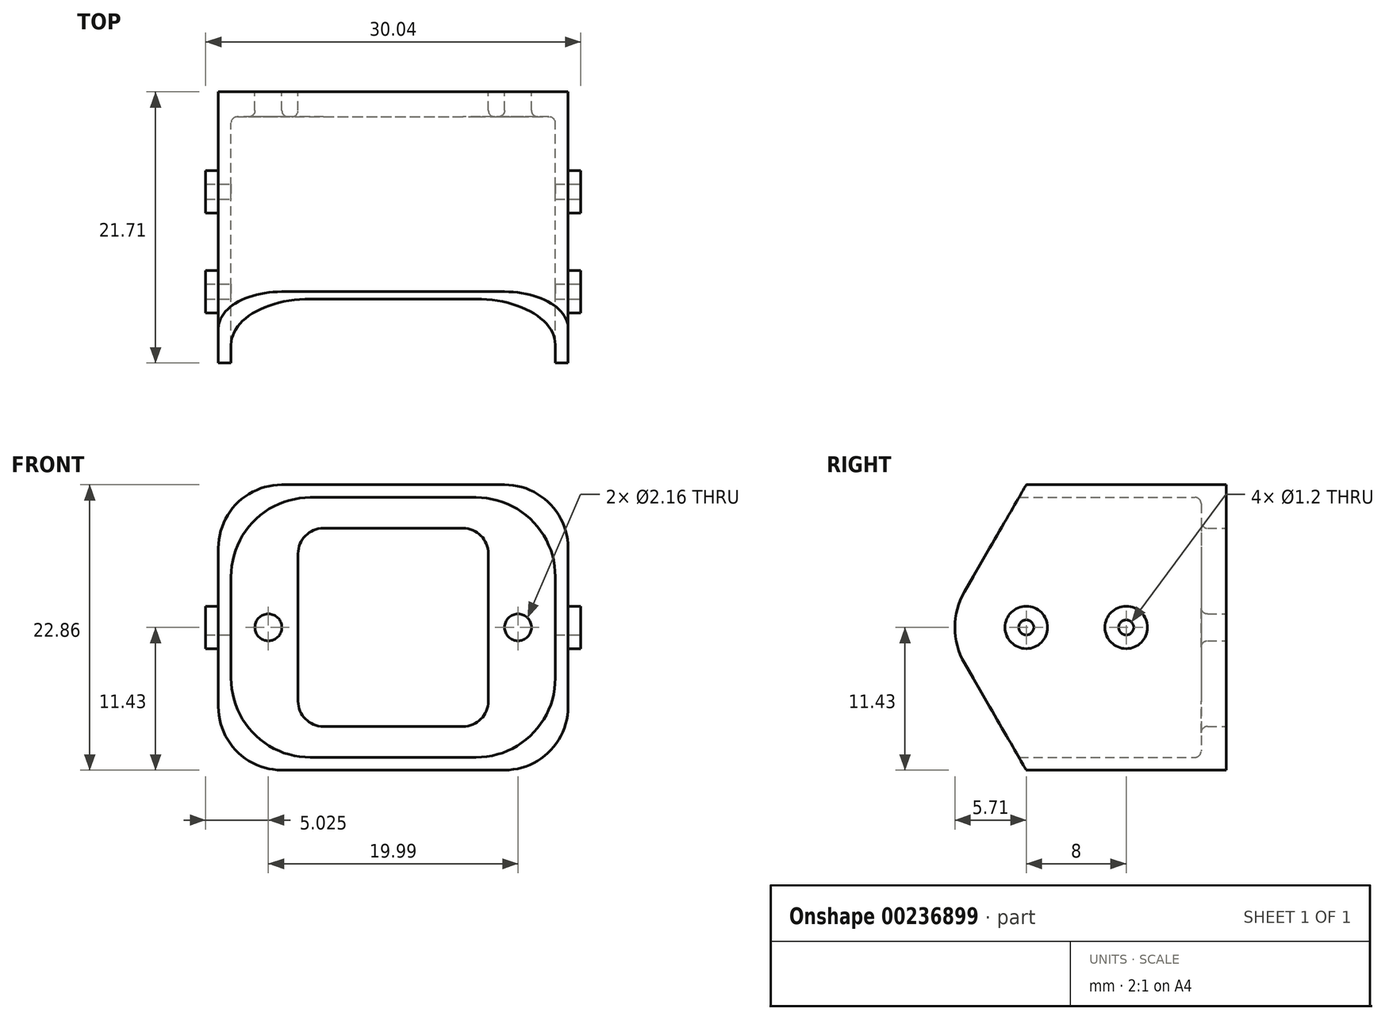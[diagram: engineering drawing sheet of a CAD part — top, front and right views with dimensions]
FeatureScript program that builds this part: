
annotation { "Feature Type Name" : "Feature", "Feature Type Description" : "" }
export const myFeature = defineFeature(function(context is Context, id is Id, definition is map)
    precondition{}
    {
        {
            var Q0;
            Q0=qCreatedBy(makeId("Front.planeOp"),FACE);
            var sketch = newSketch(context, id + "F0", { "sketchPlane" : qUnion([Q0])});
            skLineSegment(sketch, "E0.bottom", {"start": v(-8.92, 11.43) * mm, "end": v(8.92, 11.43) * mm});
            skLineSegment(sketch, "E0.top", {"start": v(-8.92, -11.43) * mm, "end": v(8.92, -11.43) * mm});
            skLineSegment(sketch, "E0.left", {"start": v(-14, 6.35) * mm, "end": v(-14, -6.35) * mm});
            skLineSegment(sketch, "E0.right", {"start": v(14, 6.35) * mm, "end": v(14, -6.35) * mm});
            skPoint(sketch, "E0.middle", {"position": v(0, 0) * mm});
            skLineSegment(sketch, "E1.bottom", {"start": v(-5.59, 7.94) * mm, "end": v(5.59, 7.94) * mm});
            skLineSegment(sketch, "E1.top", {"start": v(-5.59, -7.94) * mm, "end": v(5.59, -7.94) * mm});
            skLineSegment(sketch, "E1.left", {"start": v(-7.62, 5.9) * mm, "end": v(-7.62, -5.9) * mm});
            skLineSegment(sketch, "E1.right", {"start": v(7.62, 5.9) * mm, "end": v(7.62, -5.9) * mm});
            skCircle(sketch, "E2", {"center": v(0, 0) * mm, "radius": 10 * mm, "construction": true});
            skCircle(sketch, "E3", {"center": v(-10, 0) * mm, "radius": 1.08 * mm});
            skCircle(sketch, "E4", {"center": v(10, 0) * mm, "radius": 1.08 * mm});
            skPoint(sketch, "E4.centerSnap0", {"position": v(7.62, 0) * mm});
            skPoint(sketch, "E5.visualSharp", {"position": v(-7.62, 7.94) * mm});
            skArc(sketch, "E5.filletArc", {"start": v(-5.59, 7.94) * mm, "mid": v(-7.02, 7.34) * mm, "end": v(-7.62, 5.9) * mm});
            skPoint(sketch, "E6.visualSharp", {"position": v(7.62, 7.94) * mm});
            skArc(sketch, "E6.filletArc", {"start": v(7.62, 5.9) * mm, "mid": v(7.02, 7.34) * mm, "end": v(5.59, 7.94) * mm});
            skPoint(sketch, "E7.visualSharp", {"position": v(7.62, -7.94) * mm});
            skArc(sketch, "E7.filletArc", {"start": v(5.59, -7.94) * mm, "mid": v(7.02, -7.34) * mm, "end": v(7.62, -5.9) * mm});
            skPoint(sketch, "E8.visualSharp", {"position": v(-7.62, -7.94) * mm});
            skArc(sketch, "E8.filletArc", {"start": v(-7.62, -5.9) * mm, "mid": v(-7.02, -7.34) * mm, "end": v(-5.59, -7.94) * mm});
            skPoint(sketch, "E9.visualSharp", {"position": v(-14, 11.43) * mm});
            skArc(sketch, "E9.filletArc", {"start": v(-8.92, 11.43) * mm, "mid": v(-12.51, 9.94) * mm, "end": v(-14, 6.35) * mm});
            skPoint(sketch, "E10.visualSharp", {"position": v(-14, -11.43) * mm});
            skArc(sketch, "E10.filletArc", {"start": v(-14, -6.35) * mm, "mid": v(-12.51, -9.94) * mm, "end": v(-8.92, -11.43) * mm});
            skPoint(sketch, "E11.visualSharp", {"position": v(14, -11.43) * mm});
            skArc(sketch, "E11.filletArc", {"start": v(8.92, -11.43) * mm, "mid": v(12.51, -9.94) * mm, "end": v(14, -6.35) * mm});
            skPoint(sketch, "E12.visualSharp", {"position": v(14, 11.43) * mm});
            skArc(sketch, "E12.filletArc", {"start": v(14, 6.35) * mm, "mid": v(12.51, 9.94) * mm, "end": v(8.92, 11.43) * mm});
            skSolve(sketch);
        }
        {
            var Q0;
            Q0=qSketchRegion(id+"F0",true);
            extrude(context, id + "F1", {"entities" : qUnion([Q0]), "depth" : 2 * mm});
        }
        {
            var Q0;
            Q0=makeQuery(id+"F1.opExtrude","CAP_FACE",FACE,{"disambiguationData":[OSD([sQuery(id+"F0.wireOp",EDGE,"E0.bottom"),sQuery(id+"F0.wireOp",EDGE,"E0.top"),sQuery(id+"F0.wireOp",EDGE,"E0.left"),sQuery(id+"F0.wireOp",EDGE,"E0.right"),sQuery(id+"F0.wireOp",EDGE,"E1.bottom"),sQuery(id+"F0.wireOp",EDGE,"E1.top"),sQuery(id+"F0.wireOp",EDGE,"E1.left"),sQuery(id+"F0.wireOp",EDGE,"E1.right"),sQuery(id+"F0.wireOp",EDGE,"E3"),sQuery(id+"F0.wireOp",EDGE,"E4"),sQuery(id+"F0.wireOp",EDGE,"E5.filletArc"),sQuery(id+"F0.wireOp",EDGE,"E6.filletArc"),sQuery(id+"F0.wireOp",EDGE,"E7.filletArc"),sQuery(id+"F0.wireOp",EDGE,"E8.filletArc"),sQuery(id+"F0.wireOp",EDGE,"E9.filletArc"),sQuery(id+"F0.wireOp",EDGE,"E10.filletArc"),sQuery(id+"F0.wireOp",EDGE,"E11.filletArc"),sQuery(id+"F0.wireOp",EDGE,"E12.filletArc")])],"isStart":false});
            var sketch = newSketch(context, id + "F2", { "sketchPlane" : qUnion([Q0])});
            skLineSegment(sketch, "E13.0", {"start": v(-8.92, 11.43) * mm, "end": v(8.92, 11.43) * mm});
            skLineSegment(sketch, "E14.0", {"start": v(-14, 6.35) * mm, "end": v(-14, -6.35) * mm});
            skPoint(sketch, "E14.1", {"position": v(-12.51, 9.94) * mm});
            skArc(sketch, "E15.0", {"start": v(-8.92, 11.43) * mm, "mid": v(-12.51, 9.94) * mm, "end": v(-14, 6.35) * mm});
            skArc(sketch, "E16.0", {"start": v(14, 6.35) * mm, "mid": v(12.51, 9.94) * mm, "end": v(8.92, 11.43) * mm});
            skLineSegment(sketch, "E17.0", {"start": v(14, 6.35) * mm, "end": v(14, -6.35) * mm});
            skArc(sketch, "E18.0", {"start": v(8.92, -11.43) * mm, "mid": v(12.51, -9.94) * mm, "end": v(14, -6.35) * mm});
            skLineSegment(sketch, "E19.0", {"start": v(-8.92, -11.43) * mm, "end": v(8.92, -11.43) * mm});
            skArc(sketch, "E20.0", {"start": v(-14, -6.35) * mm, "mid": v(-12.51, -9.94) * mm, "end": v(-8.92, -11.43) * mm});
            skLineSegment(sketch, "E21.0", {"start": v(-6.64, 10.41) * mm, "end": v(6.64, 10.41) * mm});
            skLineSegment(sketch, "E22.0", {"start": v(12.99, 4.06) * mm, "end": v(12.99, -4.06) * mm});
            skLineSegment(sketch, "E23.0", {"start": v(-12.99, 4.06) * mm, "end": v(-12.99, -4.06) * mm});
            skLineSegment(sketch, "E24.0", {"start": v(-6.64, -10.41) * mm, "end": v(6.64, -10.41) * mm});
            skPoint(sketch, "E25.visualSharp", {"position": v(-12.99, 10.41) * mm});
            skArc(sketch, "E25.filletArc", {"start": v(-6.64, 10.41) * mm, "mid": v(-11.13, 8.55) * mm, "end": v(-12.99, 4.06) * mm});
            skPoint(sketch, "E26.visualSharp", {"position": v(-12.99, -10.41) * mm});
            skArc(sketch, "E26.filletArc", {"start": v(-12.99, -4.06) * mm, "mid": v(-11.13, -8.55) * mm, "end": v(-6.64, -10.41) * mm});
            skPoint(sketch, "E27.visualSharp", {"position": v(12.99, -10.41) * mm});
            skArc(sketch, "E27.filletArc", {"start": v(6.64, -10.41) * mm, "mid": v(11.13, -8.55) * mm, "end": v(12.99, -4.06) * mm});
            skPoint(sketch, "E28.visualSharp", {"position": v(12.99, 10.41) * mm});
            skArc(sketch, "E28.filletArc", {"start": v(12.99, 4.06) * mm, "mid": v(11.13, 8.55) * mm, "end": v(6.64, 10.41) * mm});
            skSolve(sketch);
        }
        {
            var Q0;
            Q0=qSketchRegion(id+"F2",true);
            extrude(context, id + "F3", {"entities" : qUnion([Q0]), "operationType" : NewBodyOperationType.ADD, "depth" : 19.99 * mm});
        }
        {
            var Q0;
            Q0=makeQuery(id+"F1.opExtrude","CAP_FACE",FACE,{"disambiguationData":[OSD([sQuery(id+"F0.wireOp",EDGE,"E0.bottom"),sQuery(id+"F0.wireOp",EDGE,"E0.top"),sQuery(id+"F0.wireOp",EDGE,"E0.left"),sQuery(id+"F0.wireOp",EDGE,"E0.right"),sQuery(id+"F0.wireOp",EDGE,"E1.bottom"),sQuery(id+"F0.wireOp",EDGE,"E1.top"),sQuery(id+"F0.wireOp",EDGE,"E1.left"),sQuery(id+"F0.wireOp",EDGE,"E1.right"),sQuery(id+"F0.wireOp",EDGE,"E3"),sQuery(id+"F0.wireOp",EDGE,"E4"),sQuery(id+"F0.wireOp",EDGE,"E5.filletArc"),sQuery(id+"F0.wireOp",EDGE,"E6.filletArc"),sQuery(id+"F0.wireOp",EDGE,"E7.filletArc"),sQuery(id+"F0.wireOp",EDGE,"E8.filletArc"),sQuery(id+"F0.wireOp",EDGE,"E9.filletArc"),sQuery(id+"F0.wireOp",EDGE,"E10.filletArc"),sQuery(id+"F0.wireOp",EDGE,"E11.filletArc"),sQuery(id+"F0.wireOp",EDGE,"E12.filletArc")])],"isStart":false});
            fillet(context, id + "F4", {"entities" : qUnion([Q0]), "radius" : 0.5 * mm, "tangentPropagation" : true, "allowEdgeOverflow" : false});
        }
        {
            var Q0;
            Q0=makeQuery(id+"F3.boolean.opBoolean","MERGE",FACE,{"derivedFrom":[makeQuery(id+"F1.opExtrude","SWEPT_FACE",FACE,{"disambiguationData":[OSD([sQuery(id+"F0.wireOp",EDGE,"E0.right")])]}),makeQuery(id+"F3.opExtrude","SWEPT_FACE",FACE,{"disambiguationData":[OSD([sQuery(id+"F2.wireOp",EDGE,"E17.0")])]})]});
            var sketch = newSketch(context, id + "F5", { "sketchPlane" : qUnion([Q0])});
            skLineSegment(sketch, "E29", {"start": v(0, 0) * mm, "end": v(-21.48, 0) * mm, "construction": true});
            skCircle(sketch, "E30", {"center": v(-8, 0) * mm, "radius": 0.6 * mm});
            skCircle(sketch, "E31", {"center": v(-16, 0) * mm, "radius": 0.6 * mm});
            skSolve(sketch);
        }
        {
            var Q0;
            Q0=qSketchRegion(id+"F5",true);
            extrude(context, id + "F6", {"entities" : qUnion([Q0]), "operationType" : NewBodyOperationType.REMOVE, "endBound" : BoundingType.THROUGH_ALL, "oppositeDirection" : true, "depth" : 25.4 * mm});
        }
        {
            var Q0;
            Q0=makeQuery(id+"F3.boolean.opBoolean","MERGE",FACE,{"derivedFrom":[makeQuery(id+"F1.opExtrude","SWEPT_FACE",FACE,{"disambiguationData":[OSD([sQuery(id+"F0.wireOp",EDGE,"E0.right")])]}),makeQuery(id+"F3.opExtrude","SWEPT_FACE",FACE,{"disambiguationData":[OSD([sQuery(id+"F2.wireOp",EDGE,"E17.0")])]})]});
            var sketch = newSketch(context, id + "F7", { "sketchPlane" : qUnion([Q0])});
            skCircle(sketch, "E32", {"center": v(-8, 0) * mm, "radius": 1.7 * mm});
            skCircle(sketch, "E33", {"center": v(-16, 0) * mm, "radius": 1.7 * mm});
            skCircle(sketch, "E34.0", {"center": v(-16, 0) * mm, "radius": 0.6 * mm});
            skCircle(sketch, "E35.0", {"center": v(-8, 0) * mm, "radius": 0.6 * mm});
            skSolve(sketch);
        }
        {
            var Q0;
            Q0=qSketchRegion(id+"F7",true);
            extrude(context, id + "F8", {"entities" : qUnion([Q0]), "operationType" : NewBodyOperationType.ADD, "depth" : 1.02 * mm});
        }
        {
            var Q0;
            Q0=makeQuery(id+"F3.boolean.opBoolean","MERGE",FACE,{"derivedFrom":[makeQuery(id+"F1.opExtrude","SWEPT_FACE",FACE,{"disambiguationData":[OSD([sQuery(id+"F0.wireOp",EDGE,"E0.left")])]}),makeQuery(id+"F3.opExtrude","SWEPT_FACE",FACE,{"disambiguationData":[OSD([sQuery(id+"F2.wireOp",EDGE,"E14.0")])]})]});
            var sketch = newSketch(context, id + "F9", { "sketchPlane" : qUnion([Q0])});
            skCircle(sketch, "E36", {"center": v(16, 0) * mm, "radius": 1.7 * mm});
            skCircle(sketch, "E37", {"center": v(8, 0) * mm, "radius": 1.7 * mm});
            skCircle(sketch, "E38.0", {"center": v(16, 0) * mm, "radius": 0.6 * mm});
            skCircle(sketch, "E39.0", {"center": v(8, 0) * mm, "radius": 0.6 * mm});
            skSolve(sketch);
        }
        {
            var Q0;
            Q0=qSketchRegion(id+"F9",true);
            extrude(context, id + "F10", {"entities" : qUnion([Q0]), "operationType" : NewBodyOperationType.ADD, "depth" : 1.02 * mm});
        }
        {
            var Q0;
            Q0=qCreatedBy(makeId("Right.planeOp"),FACE);
            var sketch = newSketch(context, id + "F11", { "sketchPlane" : qUnion([Q0])});
            skArc(sketch, "E40", {"start": v(-20.95, 2.86) * mm, "mid": v(-21.72, 0) * mm, "end": v(-20.95, -2.86) * mm});
            skLineSegment(sketch, "E41", {"start": v(-20.95, 2.86) * mm, "end": v(-14.94, 13.27) * mm});
            skLineSegment(sketch, "E42", {"start": v(-14.94, 13.27) * mm, "end": v(-27.64, 12.45) * mm});
            skLineSegment(sketch, "E43", {"start": v(-27.64, 12.45) * mm, "end": v(-27.64, -22.3) * mm});
            skLineSegment(sketch, "E44", {"start": v(-27.64, -22.3) * mm, "end": v(-9.72, -22.3) * mm});
            skLineSegment(sketch, "E45", {"start": v(-9.72, -22.3) * mm, "end": v(-20.95, -2.86) * mm});
            skSolve(sketch);
        }
        {
            var Q0;
            Q0=qSketchRegion(id+"F11",true);
            extrude(context, id + "F12", {"entities" : qUnion([Q0]), "operationType" : NewBodyOperationType.REMOVE, "endBound" : BoundingType.THROUGH_ALL, "oppositeDirection" : true, "depth" : 25.4 * mm, "hasSecondDirection" : true, "secondDirectionBound" : SecondDirectionBoundingType.THROUGH_ALL, "secondDirectionOppositeDirection" : false, "secondDirectionDepth" : 25.4 * mm});
        }
    });
